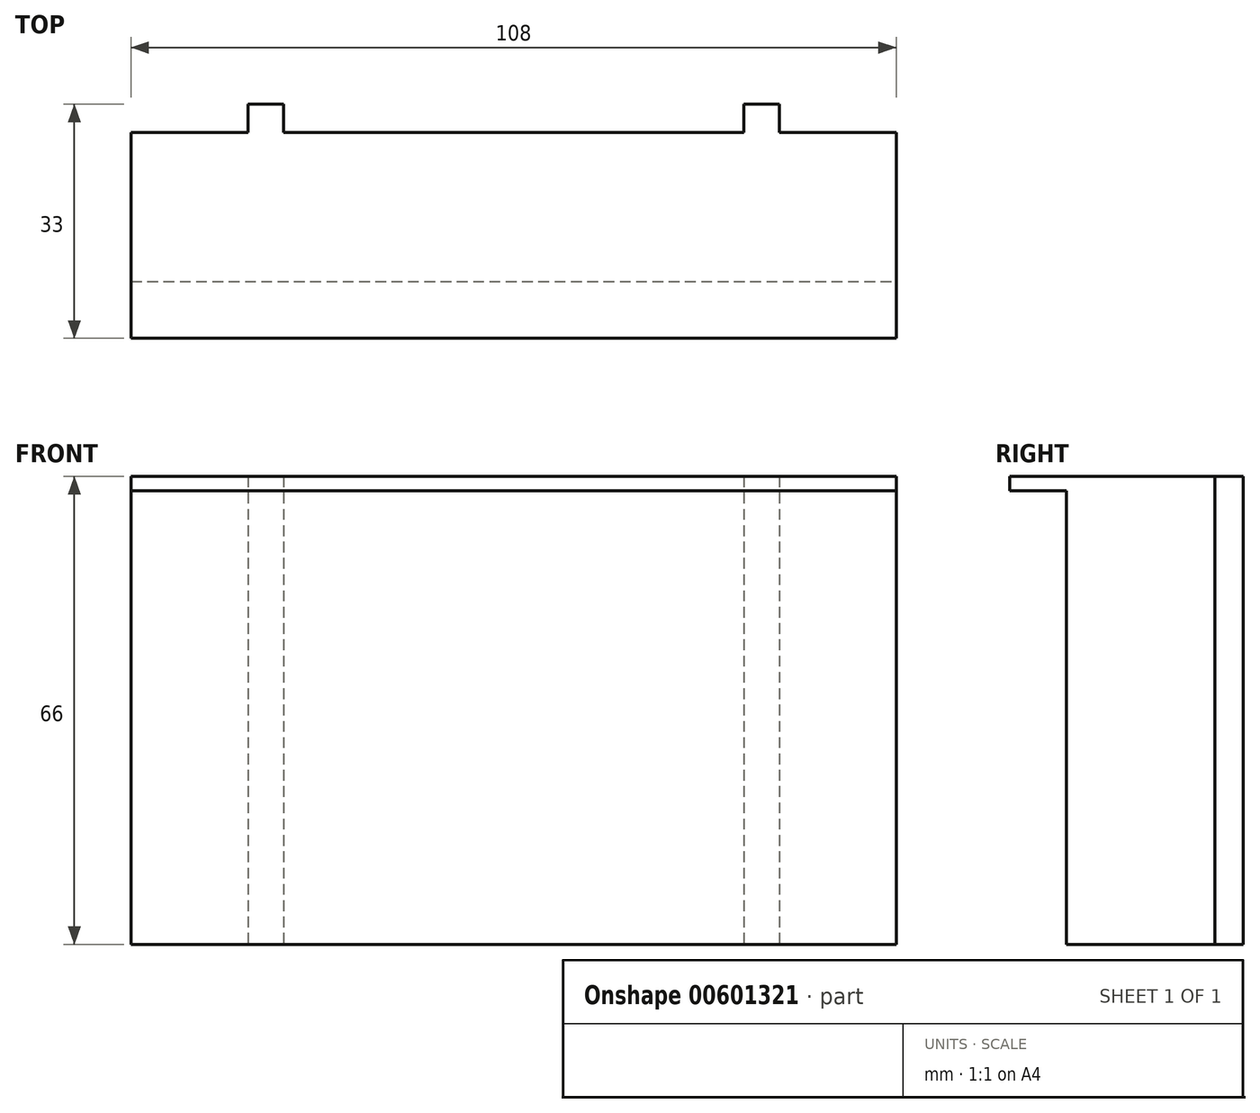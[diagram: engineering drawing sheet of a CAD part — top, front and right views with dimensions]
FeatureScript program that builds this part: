
annotation { "Feature Type Name" : "Feature", "Feature Type Description" : "" }
export const myFeature = defineFeature(function(context is Context, id is Id, definition is map)
    precondition{}
    {
        {
            var Q0;
            Q0=qCreatedBy(makeId("Front.planeOp"),FACE);
            var sketch = newSketch(context, id + "F0", { "sketchPlane" : qUnion([Q0])});
            skLineSegment(sketch, "E0.bottom", {"start": v(-54, 0) * mm, "end": v(54, 0) * mm});
            skLineSegment(sketch, "E0.top", {"start": v(-54, -66) * mm, "end": v(54, -66) * mm});
            skLineSegment(sketch, "E0.left", {"start": v(-54, 0) * mm, "end": v(-54, -66) * mm});
            skLineSegment(sketch, "E0.right", {"start": v(54, 0) * mm, "end": v(54, -66) * mm});
            skLineSegment(sketch, "E1", {"start": v(0, 0) * mm, "end": v(0, -66) * mm, "construction": true});
            skLineSegment(sketch, "E2", {"start": v(-35, 0) * mm, "end": v(-35, -66) * mm, "construction": true});
            skLineSegment(sketch, "E3.0", {"start": v(-32.5, 0) * mm, "end": v(-32.5, -66) * mm});
            skLineSegment(sketch, "E4.0", {"start": v(-37.5, 0) * mm, "end": v(-37.5, -66) * mm});
            skLineSegment(sketch, "E5", {"start": v(-37.5, 0) * mm, "end": v(-32.5, 0) * mm});
            skLineSegment(sketch, "E6", {"start": v(-37.5, -66) * mm, "end": v(-32.5, -66) * mm});
            skLineSegment(sketch, "E7.MirrorCS", {"start": v(32.5, 0) * mm, "end": v(32.5, -66) * mm});
            skLineSegment(sketch, "E8.MirrorCS", {"start": v(37.5, 0) * mm, "end": v(37.5, -66) * mm});
            skSolve(sketch);
        }
        {
            var Q0;
            Q0=makeQuery(id+"F0.imprint","IMPRINT",FACE,{"disambiguationData":[TD([[makeQuery(id+"F0.imprint","IMPRINT",EDGE,{"derivedFrom":sQuery(id+"F0.wireOp",EDGE,"E3.0")}),-1.0]])]});
            var Q1;
            {var subQ0=sQuery(id+"F0.wireOp",EDGE,"E0.left");Q1=makeQuery(id+"F0.imprint","IMPRINT",FACE,{"disambiguationData":[TD([[makeQuery(id+"F0.imprint","IMPRINT",EDGE,{"derivedFrom":subQ0}),1.0]])]});}
            var Q2;
            {var subQ0=sQuery(id+"F0.wireOp",EDGE,"E3.0");Q2=makeQuery(id+"F0.imprint","IMPRINT",FACE,{"disambiguationData":[TD([[makeQuery(id+"F0.imprint","IMPRINT",EDGE,{"derivedFrom":subQ0}),1.0]])]});}
            var Q3;
            {var subQ0=sQuery(id+"F0.wireOp",EDGE,"E7.MirrorCS");Q3=makeQuery(id+"F0.imprint","IMPRINT",FACE,{"disambiguationData":[TD([[makeQuery(id+"F0.imprint","IMPRINT",EDGE,{"derivedFrom":subQ0}),1.0]])]});}
            var Q4;
            {var subQ0=sQuery(id+"F0.wireOp",EDGE,"E0.right");Q4=makeQuery(id+"F0.imprint","IMPRINT",FACE,{"disambiguationData":[TD([[makeQuery(id+"F0.imprint","IMPRINT",EDGE,{"derivedFrom":subQ0}),-1.0]])]});}
            extrude(context, id + "F1", {"entities" : qUnion([Q0, Q1, Q2, Q3, Q4]), "depth" : 21 * mm, "offsetDistance" : 25 * mm});
        }
        {
            var Q0;
            {var subQ0=sQuery(id+"F0.wireOp",EDGE,"E7.MirrorCS");Q0=makeQuery(id+"F0.imprint","IMPRINT",FACE,{"disambiguationData":[TD([[makeQuery(id+"F0.imprint","IMPRINT",EDGE,{"derivedFrom":subQ0}),1.0]])]});}
            var Q1;
            Q1=makeQuery(id+"F0.imprint","IMPRINT",FACE,{"disambiguationData":[TD([[makeQuery(id+"F0.imprint","IMPRINT",EDGE,{"derivedFrom":sQuery(id+"F0.wireOp",EDGE,"E3.0")}),-1.0]])]});
            extrude(context, id + "F2", {"entities" : qUnion([Q0, Q1]), "operationType" : NewBodyOperationType.ADD, "oppositeDirection" : true, "depth" : 4 * mm, "offsetDistance" : 25 * mm});
        }
        {
            var Q0;
            Q0=makeQuery(id+"F1.opExtrude","CAP_FACE",FACE,{"disambiguationData":[OSD([sQuery(id+"F0.wireOp",EDGE,"E0.bottom"),sQuery(id+"F0.wireOp",EDGE,"E0.top"),sQuery(id+"F0.wireOp",EDGE,"E0.left"),sQuery(id+"F0.wireOp",EDGE,"E0.right"),sQuery(id+"F0.wireOp",EDGE,"E5"),sQuery(id+"F0.wireOp",EDGE,"E6")])],"isStart":false});
            var sketch = newSketch(context, id + "F3", { "sketchPlane" : qUnion([Q0])});
            skLineSegment(sketch, "E9.bottom", {"start": v(-54, 0) * mm, "end": v(54, 0) * mm});
            skLineSegment(sketch, "E9.top", {"start": v(-54, -2) * mm, "end": v(54, -2) * mm});
            skLineSegment(sketch, "E9.left", {"start": v(-54, 0) * mm, "end": v(-54, -2) * mm});
            skLineSegment(sketch, "E9.right", {"start": v(54, 0) * mm, "end": v(54, -2) * mm});
            skSolve(sketch);
        }
        {
            var Q0;
            Q0 = qSketchRegion(id + "F3", true);
            extrude(context, id + "F4", {"entities" : qUnion([Q0]), "operationType" : NewBodyOperationType.ADD, "depth" : 8 * mm, "offsetDistance" : 25 * mm});
        }
    });
